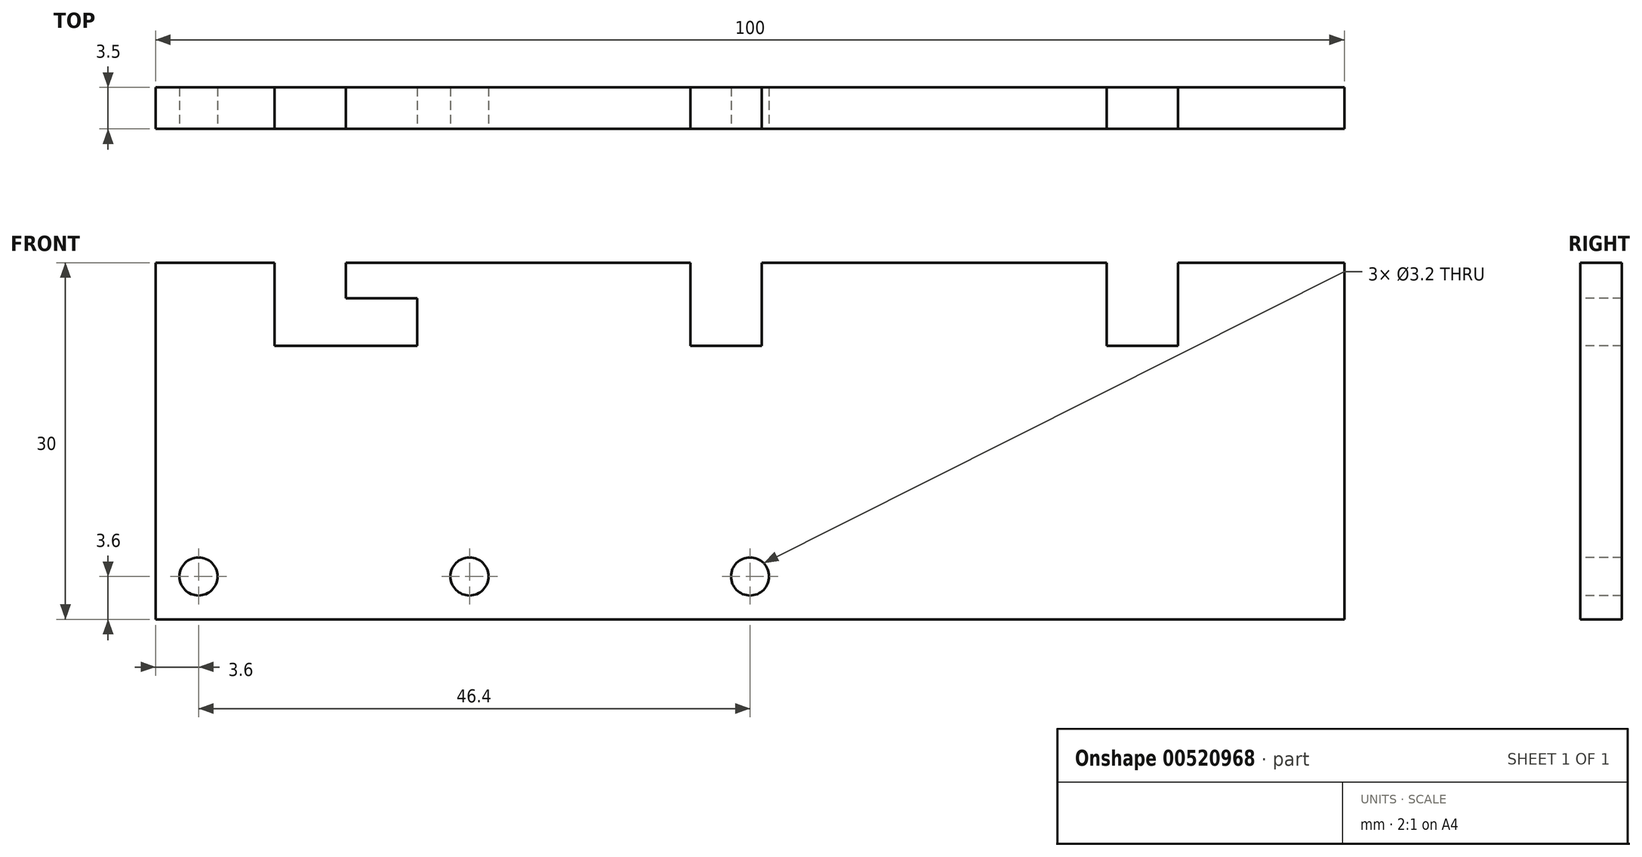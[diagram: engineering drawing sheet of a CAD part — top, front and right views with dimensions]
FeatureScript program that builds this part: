
annotation { "Feature Type Name" : "Feature", "Feature Type Description" : "" }
export const myFeature = defineFeature(function(context is Context, id is Id, definition is map)
    precondition{}
    {
        {
            var Q0;
            Q0=qCreatedBy(makeId("Front.planeOp"),FACE);
            var sketch = newSketch(context, id + "F0", { "sketchPlane" : qUnion([Q0])});
            skLineSegment(sketch, "E0.bottom", {"start": v(50, -15) * mm, "end": v(-50, -15) * mm});
            skLineSegment(sketch, "E0.top", {"start": v(50, 15) * mm, "end": v(-50, 15) * mm});
            skLineSegment(sketch, "E0.left", {"start": v(50, -15) * mm, "end": v(50, 15) * mm});
            skLineSegment(sketch, "E0.right", {"start": v(-50, -15) * mm, "end": v(-50, 15) * mm});
            skPoint(sketch, "E0.middle", {"position": v(0, 0) * mm});
            skSolve(sketch);
        }
        {
            var Q0;
            Q0 = qSketchRegion(id + "F0", true);
            extrude(context, id + "F1", {"entities" : qUnion([Q0]), "depth" : 3.5 * mm, "offsetDistance" : 25 * mm});
        }
        {
            var Q0;
            Q0=makeQuery(id+"F1.opExtrude","CAP_FACE",FACE,{"disambiguationData":[OSD([sQuery(id+"F0.wireOp",EDGE,"E0.bottom"),sQuery(id+"F0.wireOp",EDGE,"E0.top"),sQuery(id+"F0.wireOp",EDGE,"E0.left"),sQuery(id+"F0.wireOp",EDGE,"E0.right")])],"isStart":false});
            var sketch = newSketch(context, id + "F2", { "sketchPlane" : qUnion([Q0])});
            skLineSegment(sketch, "E1.bottom", {"start": v(-50, -15) * mm, "end": v(-23.6, -15) * mm});
            skLineSegment(sketch, "E1.top", {"start": v(-50, -11.4) * mm, "end": v(-23.6, -11.4) * mm});
            skLineSegment(sketch, "E1.left", {"start": v(-50, -15) * mm, "end": v(-50, -11.4) * mm});
            skLineSegment(sketch, "E1.right", {"start": v(-23.6, -15) * mm, "end": v(-23.6, -11.4) * mm});
            skCircle(sketch, "E2", {"center": v(-23.6, -11.4) * mm, "radius": 1.6 * mm});
            skLineSegment(sketch, "E3", {"start": v(-25.2, -11.4) * mm, "end": v(-44.8, -11.4) * mm});
            skLineSegment(sketch, "E4", {"start": v(-50, -11.4) * mm, "end": v(-48, -11.4) * mm});
            skCircle(sketch, "E5", {"center": v(-46.4, -11.4) * mm, "radius": 1.6 * mm});
            skPoint(sketch, "E5.third.point", {"position": v(-46.26, -13) * mm});
            skLineSegment(sketch, "E6", {"start": v(-23.6, -11.4) * mm, "end": v(0, -11.4) * mm});
            skCircle(sketch, "E7", {"center": v(0, -11.4) * mm, "radius": 1.6 * mm});
            skSolve(sketch);
        }
        {
            var Q0;
            {var subQ0=sQuery(id+"F2.wireOp",EDGE,"E5");var subQ1=sQuery(id+"F2.wireOp",EDGE,"E1.top");var subQ2=makeQuery(id+"F2.imprint","INTERSECT",VERTEX,{"derivedFrom":[subQ1,sQuery(id+"F2.wireOp",EDGE,"E4"),subQ0]});Q0=makeQuery(id+"F2.imprint","IMPRINT",FACE,{"disambiguationData":[TD([[makeQuery(id+"F2.imprint","IMPRINT",EDGE,{"disambiguationData":[TD([[subQ2,-1.0]])],"derivedFrom":subQ1}),1.0]])]});}
            var Q1;
            {var subQ0=sQuery(id+"F2.wireOp",EDGE,"E5");var subQ1=sQuery(id+"F2.wireOp",EDGE,"E1.top");var subQ2=makeQuery(id+"F2.imprint","INTERSECT",VERTEX,{"derivedFrom":[subQ1,sQuery(id+"F2.wireOp",EDGE,"E4"),subQ0]});Q1=makeQuery(id+"F2.imprint","IMPRINT",FACE,{"disambiguationData":[TD([[makeQuery(id+"F2.imprint","IMPRINT",EDGE,{"disambiguationData":[TD([[subQ2,-1.0]])],"derivedFrom":subQ1}),-1.0]])]});}
            var Q2;
            {var subQ0=sQuery(id+"F2.wireOp",EDGE,"E1.right");var subQ1=sQuery(id+"F2.wireOp",EDGE,"E1.top");var subQ2=makeQuery(id+"F2.imprint","INTERSECT",VERTEX,{"derivedFrom":[subQ1,subQ0]});Q2=makeQuery(id+"F2.imprint","IMPRINT",FACE,{"disambiguationData":[TD([[makeQuery(id+"F2.imprint","IMPRINT",EDGE,{"disambiguationData":[TD([[subQ2,1.0]])],"derivedFrom":subQ0}),-1.0]])]});}
            var Q3;
            {var subQ0=sQuery(id+"F2.wireOp",EDGE,"E1.right");var subQ1=sQuery(id+"F2.wireOp",EDGE,"E1.top");var subQ2=makeQuery(id+"F2.imprint","INTERSECT",VERTEX,{"derivedFrom":[subQ1,subQ0]});Q3=makeQuery(id+"F2.imprint","IMPRINT",FACE,{"disambiguationData":[TD([[makeQuery(id+"F2.imprint","IMPRINT",EDGE,{"disambiguationData":[TD([[subQ2,1.0]])],"derivedFrom":subQ0}),1.0]])]});}
            var Q4;
            {var subQ0=sQuery(id+"F2.wireOp",EDGE,"E6");var subQ3=sQuery(id+"F2.wireOp",EDGE,"E2");var subQ5=makeQuery(id+"F2.imprint","INTERSECT",VERTEX,{"derivedFrom":[subQ3,subQ0]});Q4=makeQuery(id+"F2.imprint","IMPRINT",FACE,{"disambiguationData":[TD([[makeQuery(id+"F2.imprint","IMPRINT",EDGE,{"disambiguationData":[TD([[subQ5,-1.0]])],"derivedFrom":subQ3}),1.0]])]});}
            var Q5;
            Q5=makeQuery(id+"F2.imprint","IMPRINT",FACE,{"disambiguationData":[TD([[makeQuery(id+"F2.imprint","IMPRINT",EDGE,{"derivedFrom":sQuery(id+"F2.wireOp",EDGE,"E7")}),1.0]])]});
            extrude(context, id + "F3", {"entities" : qUnion([Q0, Q1, Q2, Q3, Q4, Q5]), "operationType" : NewBodyOperationType.REMOVE, "endBound" : BoundingType.THROUGH_ALL, "oppositeDirection" : true, "depth" : 25 * mm, "offsetDistance" : 25 * mm});
        }
        {
            var Q0;
            Q0=makeQuery(id+"F1.opExtrude","CAP_FACE",FACE,{"disambiguationData":[OSD([sQuery(id+"F0.wireOp",EDGE,"E0.bottom"),sQuery(id+"F0.wireOp",EDGE,"E0.top"),sQuery(id+"F0.wireOp",EDGE,"E0.left"),sQuery(id+"F0.wireOp",EDGE,"E0.right")])],"isStart":false});
            var sketch = newSketch(context, id + "F4", { "sketchPlane" : qUnion([Q0])});
            skLineSegment(sketch, "E8", {"start": v(-50, 15) * mm, "end": v(-40, 15) * mm});
            skLineSegment(sketch, "E9.bottom", {"start": v(-40, 15) * mm, "end": v(-34, 15) * mm});
            skLineSegment(sketch, "E9.top", {"start": v(-40, 8) * mm, "end": v(-34, 8) * mm});
            skLineSegment(sketch, "E9.left", {"start": v(-40, 15) * mm, "end": v(-40, 8) * mm});
            skLineSegment(sketch, "E9.right", {"start": v(-34, 15) * mm, "end": v(-34, 8) * mm});
            skLineSegment(sketch, "E10.bottom", {"start": v(-34, 8) * mm, "end": v(-28, 8) * mm});
            skLineSegment(sketch, "E10.top", {"start": v(-34, 12) * mm, "end": v(-28, 12) * mm});
            skLineSegment(sketch, "E10.left", {"start": v(-34, 8) * mm, "end": v(-34, 12) * mm});
            skLineSegment(sketch, "E10.right", {"start": v(-28, 8) * mm, "end": v(-28, 12) * mm});
            skLineSegment(sketch, "E11", {"start": v(-34, 15) * mm, "end": v(-5, 15) * mm});
            skLineSegment(sketch, "E12", {"start": v(-28, 8) * mm, "end": v(50, 8) * mm});
            skLineSegment(sketch, "E13.bottom", {"start": v(-5, 15) * mm, "end": v(1, 15) * mm});
            skLineSegment(sketch, "E13.top", {"start": v(-5, 8) * mm, "end": v(1, 8) * mm});
            skLineSegment(sketch, "E13.left", {"start": v(-5, 15) * mm, "end": v(-5, 8) * mm});
            skLineSegment(sketch, "E13.right", {"start": v(1, 15) * mm, "end": v(1, 8) * mm});
            skLineSegment(sketch, "E14.bottom", {"start": v(1, 8) * mm, "end": v(7, 8) * mm});
            skLineSegment(sketch, "E14.top", {"start": v(1, 12) * mm, "end": v(7, 12) * mm});
            skLineSegment(sketch, "E14.left", {"start": v(1, 8) * mm, "end": v(1, 12) * mm});
            skLineSegment(sketch, "E14.right", {"start": v(7, 8) * mm, "end": v(7, 12) * mm});
            skLineSegment(sketch, "E15", {"start": v(1, 15) * mm, "end": v(30, 15) * mm});
            skLineSegment(sketch, "E16.bottom", {"start": v(30, 15) * mm, "end": v(36, 15) * mm});
            skLineSegment(sketch, "E16.top", {"start": v(30, 8) * mm, "end": v(36, 8) * mm});
            skLineSegment(sketch, "E16.left", {"start": v(30, 15) * mm, "end": v(30, 8) * mm});
            skLineSegment(sketch, "E16.right", {"start": v(36, 15) * mm, "end": v(36, 8) * mm});
            skLineSegment(sketch, "E17.bottom", {"start": v(36, 8) * mm, "end": v(42, 8) * mm});
            skLineSegment(sketch, "E17.top", {"start": v(36, 12) * mm, "end": v(42, 12) * mm});
            skLineSegment(sketch, "E17.left", {"start": v(36, 8) * mm, "end": v(36, 12) * mm});
            skLineSegment(sketch, "E17.right", {"start": v(42, 8) * mm, "end": v(42, 12) * mm});
            skSolve(sketch);
        }
        {
            var Q0;
            Q0=makeQuery(id+"F4.imprint","IMPRINT",FACE,{"disambiguationData":[TD([[makeQuery(id+"F4.imprint","IMPRINT",EDGE,{"derivedFrom":sQuery(id+"F4.wireOp",EDGE,"E9.bottom")}),1.0]])]});
            var Q1;
            Q1=makeQuery(id+"F4.imprint","IMPRINT",FACE,{"disambiguationData":[TD([[makeQuery(id+"F4.imprint","IMPRINT",EDGE,{"derivedFrom":sQuery(id+"F4.wireOp",EDGE,"E10.bottom")}),1.0]])]});
            var Q2;
            Q2=makeQuery(id+"F4.imprint","IMPRINT",FACE,{"disambiguationData":[TD([[makeQuery(id+"F4.imprint","IMPRINT",EDGE,{"derivedFrom":sQuery(id+"F4.wireOp",EDGE,"E13.bottom")}),1.0]])]});
            var Q3;
            Q3=makeQuery(id+"F4.imprint","IMPRINT",FACE,{"disambiguationData":[TD([[makeQuery(id+"F4.imprint","IMPRINT",EDGE,{"derivedFrom":sQuery(id+"F4.wireOp",EDGE,"E14.bottom")}),1.0]])]});
            var Q4;
            Q4=makeQuery(id+"F4.imprint","IMPRINT",FACE,{"disambiguationData":[TD([[makeQuery(id+"F4.imprint","IMPRINT",EDGE,{"derivedFrom":sQuery(id+"F4.wireOp",EDGE,"E16.bottom")}),1.0]])]});
            var Q5;
            Q5=makeQuery(id+"F4.imprint","IMPRINT",FACE,{"disambiguationData":[TD([[makeQuery(id+"F4.imprint","IMPRINT",EDGE,{"derivedFrom":sQuery(id+"F4.wireOp",EDGE,"E17.bottom")}),1.0]])]});
            extrude(context, id + "F5", {"entities" : qUnion([Q0, Q1, Q2, Q3, Q4, Q5]), "operationType" : NewBodyOperationType.REMOVE, "endBound" : BoundingType.THROUGH_ALL, "oppositeDirection" : true, "depth" : -3.5 * mm, "offsetDistance" : 25 * mm});
        }
    });
